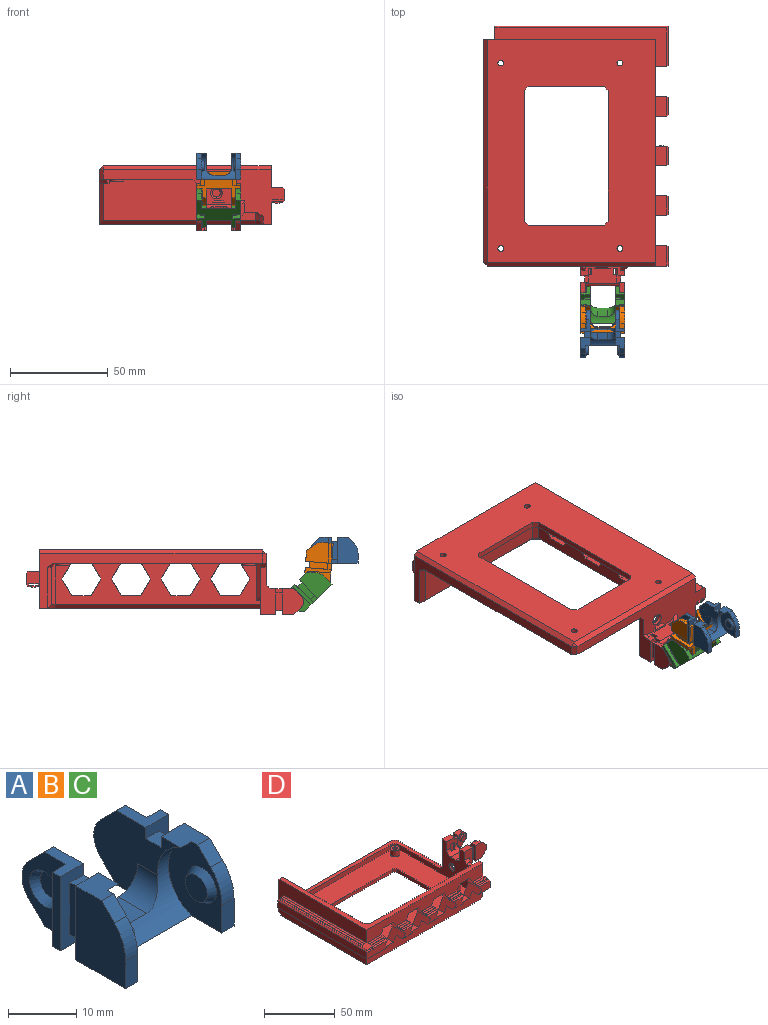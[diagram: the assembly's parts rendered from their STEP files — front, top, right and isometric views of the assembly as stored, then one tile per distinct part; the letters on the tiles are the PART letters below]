
ASSEMBLY  parts=4 mates=3
PART A: 54 faces, bbox 22.5x24.4x13.3 mm
  f0: plane 9.3x3.2mm, normal (-1,0,0), area 29.8mm2, adj f16,f17,f51,f53
  f1: plane 5.35x4.75mm, normal (0,0,1), area 22.5mm2, adj f4,f9,f17,f18,f40,f41
  f2: plane 9.3x3.2mm, normal (1,0,0), area 29.8mm2, adj f24,f25,f49,f52
  f3: plane 5.35x4.75mm, normal (0,0,1), area 22.5mm2, adj f5,f23,f24,f27,f39,f41
  f4: plane 18.07x13.3mm, normal (1,0,0), area 130.5mm2, adj f1,f6,f11,f16,f17,f19,f31,f32
  f5: plane 18.07x13.3mm, normal (-1,0,0), area 130.5mm2, adj f3,f6,f11,f24,f25,f26,f29,f30
  f6: plane 22.5x19.65mm, normal (0,0,-1), area 224.2mm2, adj f4,f5,f7,f8,f11,f13,f14,f15
  f7: plane 4.99x2.5mm, normal (0,-1,0), area 12.5mm2, adj f6,f23,f28,f39
  f8: plane 4.99x2.5mm, normal (0,-1,0), area 12.5mm2, adj f6,f10,f18,f40
  f9: plane 2.66x2.66mm, normal (0,-0.71,0.71), area 9.4mm2, adj f1,f10,f18,f40
  f10: cylinder r=8mm len=5.66mm, axis (1,0,0), area 15.7mm2, adj f8,f9,f18,f40
  f11: plane 13x6mm, normal (0,1,0), area 32.9mm2, adj f4,f5,f6,f12,f35,f36
  f12: plane 5.92x5mm, normal (0,0,1), area 29.6mm2, adj f11,f35,f36,f41
  f13: plane 13.3x9.1mm, normal (-1,0,0), area 67.8mm2, adj f6,f14,f19,f31,f32,f33,f44
  f14: plane 13.3x2.85mm, normal (0,1,0), area 37.9mm2, adj f6,f13,f15,f19
  f15: plane 13.3x1.7mm, normal (-1,0,0), area 22.6mm2, adj f6,f14,f16,f19
  f16: plane 13.3x4.75mm, normal (0,-1,0), area 36.1mm2, adj f0,f4,f6,f15,f19,f50,f51,f53
  f17: plane 13.3x4.75mm, normal (0,1,0), area 36.1mm2, adj f0,f1,f4,f6,f18,f50,f51,f53
  f18: plane 13.3x10.35mm, normal (-1,0,0), area 123.8mm2, adj f1,f6,f8,f9,f10,f17
  f19: plane 6.1x4.75mm, normal (0,0,1), area 16.4mm2, adj f4,f13,f14,f15,f16,f31
  f20: plane 13.3x1.7mm, normal (1,0,0), area 22.6mm2, adj f6,f21,f25,f26
  f21: plane 13.3x2.85mm, normal (0,1,0), area 37.9mm2, adj f6,f20,f22,f26
  f22: plane 13.3x9.1mm, normal (1,0,0), area 67.8mm2, adj f6,f21,f26,f29,f30,f34,f37
  f23: plane 13.3x10.35mm, normal (1,0,0), area 123.8mm2, adj f3,f6,f7,f24,f27,f28
  f24: plane 13.3x4.75mm, normal (0,1,0), area 36.1mm2, adj f2,f3,f5,f6,f23,f48,f49,f52
  f25: plane 13.3x4.75mm, normal (0,-1,0), area 36.1mm2, adj f2,f5,f6,f20,f26,f48,f49,f52
  f26: plane 6.1x4.75mm, normal (0,0,1), area 16.4mm2, adj f5,f20,f21,f22,f25,f29
  f27: plane 2.66x2.66mm, normal (0,-0.71,0.71), area 9.4mm2, adj f3,f23,f28,f39
  f28: cylinder r=8mm len=5.66mm, axis (1,0,0), area 15.7mm2, adj f7,f23,f27,f39
  f29: plane 3.33x3.33mm, normal (0,0.71,0.71), area 8.9mm2, adj f5,f22,f26,f34
  f30: plane 3.33x3.33mm, normal (0,0.71,-0.71), area 8.9mm2, adj f5,f6,f22,f34
  f31: plane 3.33x3.33mm, normal (0,0.71,0.71), area 8.9mm2, adj f4,f13,f19,f33
  f32: plane 3.33x3.33mm, normal (0,0.71,-0.71), area 8.9mm2, adj f4,f6,f13,f33
  f33: cylinder r=4.7mm len=6.65mm, axis (-1,0,0), area 14mm2, adj f4,f13,f31,f32
  f34: cylinder r=4.7mm len=6.65mm, axis (-1,0,0), area 14mm2, adj f5,f22,f29,f30
  f35: cylinder r=4mm len=5.92mm, axis (0,1,0), area 31.9mm2, adj f4,f11,f12,f41
  f36: cylinder r=4mm len=5.92mm, axis (0,-1,0), area 31.9mm2, adj f5,f11,f12,f41
  f37: cone r=3.1mm half-angle=30deg, axis (1,0,0), area 27.4mm2, adj f22,f38
  f38: plane 4.58x4.58mm, normal (1,0,0), area 16.5mm2, adj f37
  f39: plane 13.3x11.1mm, normal (-1,0,0), area 88.3mm2, adj f3,f6,f7,f27,f28,f41,f42
  f40: plane 13.3x11.1mm, normal (1,0,0), area 88.3mm2, adj f1,f6,f8,f9,f10,f41,f46
  f41: cylinder r=7mm len=17.5mm, axis (1,0,0), area 135.2mm2, adj f1,f3,f4,f5,f6,f12,f35,f36
  f42: cone r=3mm half-angle=30deg, axis (1,0,0), area 23.9mm2, adj f39,f43
  f43: plane 4.56x4.56mm, normal (-1,0,0), area 16.3mm2, adj f42
  f44: cone r=3.1mm half-angle=30deg, axis (-1,0,0), area 27.4mm2, adj f13,f45
  f45: plane 4.58x4.58mm, normal (-1,0,0), area 16.5mm2, adj f44
  f46: cone r=3mm half-angle=30deg, axis (-1,0,0), area 23.9mm2, adj f40,f47
  f47: plane 4.56x4.56mm, normal (1,0,0), area 16.3mm2, adj f46
  f48: plane 3.2x2mm, normal (1,0,0), area 6.4mm2, adj f6,f24,f25,f49
  f49: plane 3.2x2mm, normal (0,0,-1), area 6.4mm2, adj f2,f24,f25,f48
  f50: plane 3.2x2mm, normal (-1,0,0), area 6.4mm2, adj f6,f16,f17,f51
  f51: plane 3.2x2mm, normal (0,0,-1), area 6.4mm2, adj f0,f16,f17,f50
  f52: plane 3.2x2.75mm, normal (0,0,1), area 8.8mm2, adj f2,f5,f24,f25
  f53: plane 3.2x2.75mm, normal (0,0,1), area 8.8mm2, adj f0,f4,f16,f17
PART B: same geometry as A
PART C: same geometry as A
PART D: 229 faces, bbox 142.5x95.3x35.7 mm
  f0: plane 9.3x1.7mm, normal (1,0,0), area 11.3mm2, adj f1,f2,f8,f9,f10,f207,f212
  f1: plane 3.53x3.4mm, normal (0,-1,0), area 12mm2, adj f0,f8,f10,f208
  f2: plane 8.5x3.4mm, normal (0,1,0), area 28.9mm2, adj f0,f8,f208,f212
  f3: plane 3.53x3.4mm, normal (0,1,0), area 12mm2, adj f4,f8,f186,f210
  f4: plane 9.3x1.7mm, normal (1,0,0), area 11.3mm2, adj f3,f5,f8,f175,f186,f209,f211
  f5: plane 8.5x3.4mm, normal (0,-1,0), area 28.9mm2, adj f4,f8,f210,f211
  f6: plane 2.4x2mm, normal (0.71,0,-0.71), area 4mm2, adj f8,f43,f167,f221
  f7: plane 4.4x2mm, normal (0.71,0,-0.71), area 6.8mm2, adj f8,f43,f214,f222
  f8: plane 22.5x14.2mm, normal (0,0,-1), area 168.2mm2, adj f0,f1,f2,f3,f4,f5,f6,f7
  f9: plane 13.84x7.3mm, normal (0,1,0), area 64mm2, adj f0,f10,f18,f55,f168,f171,f172,f185
  f10: cylinder r=4mm len=12.06mm, axis (-1,0,0), area 62.5mm2, adj f0,f1,f9,f55,f178,f197,f198,f208
  f11: plane 2.5x0.03mm, normal (1,0,0), area 0.1mm2, adj f14,f15,f169,f194
  f12: plane 3.84x3.84mm, normal (0.71,0,0.71), area 13.6mm2, adj f14,f18,f169,f194
  f13: plane 3.84x3.84mm, normal (0.71,0,-0.71), area 13.6mm2, adj f8,f15,f169,f194
  f14: cylinder r=3.95mm len=2.79mm, axis (0,1,0), area 7.8mm2, adj f11,f12,f169,f194
  f15: cylinder r=3.95mm len=2.79mm, axis (0,1,0), area 7.8mm2, adj f11,f13,f169,f194
  f16: plane 9.3x3.2mm, normal (0,-1,0), area 29.8mm2, adj f168,f171,f184,f185
  f17: plane 9.3x3.2mm, normal (0,1,0), area 29.8mm2, adj f173,f174,f180,f182
  f18: plane 6.32x5.07mm, normal (0,0,1), area 25.1mm2, adj f9,f12,f168,f169,f193,f194,f196
  f19: plane 6.32x5.07mm, normal (0,0,1), area 25.1mm2, adj f173,f175,f176,f187,f191,f195,f202
  f20: plane 106x25mm, normal (0,1,0), area 1541.8mm2, adj f42,f67,f68,f69,f70,f71,f72,f73
  f21: plane 20.13x6mm, normal (0,-1,0), area 112.6mm2, adj f85,f90,f105,f106,f108,f141,f164,f165
  f22: plane 88x19.71mm, normal (0,0,1), area 380.6mm2, adj f23,f31,f40,f45,f90,f104,f106,f107
  f23: plane 13.83x0.2mm, normal (0,-0.71,0.71), area 3.9mm2, adj f22,f27,f90,f138
  f24: plane 10.25x0.2mm, normal (0,-0.71,0.71), area 2.9mm2, adj f28,f35,f84,f88
  f25: plane 10.25x0.2mm, normal (0,-0.71,0.71), area 2.9mm2, adj f29,f36,f73,f82
  f26: plane 10.25x0.2mm, normal (0,-0.71,0.71), area 2.9mm2, adj f30,f37,f72,f77
  f27: plane 13.83x2mm, normal (0,0,1), area 27.6mm2, adj f23,f31,f90,f138
  f28: plane 10.25x2mm, normal (0,0,1), area 20.5mm2, adj f24,f32,f84,f88
  f29: plane 10.25x2mm, normal (0,0,1), area 20.5mm2, adj f25,f33,f73,f82
  f30: plane 10.25x2mm, normal (0,0,1), area 20.5mm2, adj f26,f34,f72,f77
  f31: plane 13.83x0.2mm, normal (0,0.71,0.71), area 3.9mm2, adj f22,f27,f90,f138
  f32: plane 10.25x0.2mm, normal (0,0.71,0.71), area 2.9mm2, adj f28,f84,f88,f92
  f33: plane 10.25x0.2mm, normal (0,0.71,0.71), area 2.9mm2, adj f29,f73,f82,f95
  f34: plane 10.25x0.2mm, normal (0,0.71,0.71), area 2.9mm2, adj f30,f72,f77,f98
  f35: plane 10.02x1.6mm, normal (0,0,1), area 16mm2, adj f24,f84,f88,f110
  f36: plane 10.02x1.6mm, normal (0,0,1), area 16mm2, adj f25,f73,f82,f113
  f37: plane 10.02x1.6mm, normal (0,0,1), area 16mm2, adj f26,f72,f77,f114
  f38: plane 10.71x1.6mm, normal (0,0,1), area 17.1mm2, adj f43,f70,f117,f135
  f39: plane 116x88mm, normal (0,0,1), area 808mm2, adj f40,f43,f44,f45,f120,f122,f123
  f40: plane 116x11mm, normal (0,-1,0), area 1039.4mm2, adj f22,f39,f43,f45,f70,f71,f72,f73
  f41: plane 116x11mm, normal (0,-1,0), area 1037.4mm2, adj f43,f45,f54,f67,f68,f69,f74,f75
  f42: plane 107x79mm, normal (0,0,1), area 5246.1mm2, adj f20,f46,f47,f48,f52,f55,f56,f58
  f43: plane 93x28mm, normal (1,0,0), area 1006.8mm2, adj f6,f7,f8,f38,f39,f40,f41,f57
  f44: plane 114x28mm, normal (0,1,0), area 664.8mm2, adj f39,f45,f57,f119,f125,f126,f219
  f45: plane 88x30mm, normal (-1,0,0), area 1982mm2, adj f22,f39,f40,f41,f44,f54,f91,f104
  f46: plane 67x3mm, normal (0,1,0), area 201mm2, adj f42,f54,f131,f133
  f47: plane 39x3mm, normal (1,0,0), area 117mm2, adj f42,f54,f131,f132
  f48: plane 67x3mm, normal (0,-1,0), area 201mm2, adj f42,f54,f132,f134
  f49: cylinder r=1.5mm len=8mm, axis (0,0,1), area 75.4mm2, adj f54,f63
  f50: cylinder r=1.5mm len=8mm, axis (0,0,1), area 75.4mm2, adj f54,f61
  f51: cylinder r=1.5mm len=8mm, axis (0,0,1), area 75.4mm2, adj f54,f59
  f52: plane 39x3mm, normal (-1,0,0), area 117mm2, adj f42,f54,f133,f134
  f53: cylinder r=1.5mm len=8mm, axis (0,0,1), area 75.4mm2, adj f54,f65
  f54: plane 114x86mm, normal (0,0,-1), area 6730.7mm2, adj f41,f45,f46,f47,f48,f49,f50,f51
  f55: plane 75x30.3mm, normal (-1,0,0), area 854.9mm2, adj f9,f10,f42,f57,f118,f130,f166,f167
  f56: plane 103x4mm, normal (0,-1,0), area 412mm2, adj f42,f57,f129,f130
  f57: plane 109.17x48mm, normal (0,0,1), area 459.7mm2, adj f43,f44,f55,f56,f125,f130,f218,f219
  f58: cylinder r=3.5mm len=7mm, axis (0,0,-1), area 110mm2, adj f42,f59
  f59: plane 7x7mm, normal (0,0,1), area 31.4mm2, adj f51,f58
  f60: cylinder r=3.5mm len=7mm, axis (0,0,-1), area 110mm2, adj f42,f61
  f61: plane 7x7mm, normal (0,0,1), area 31.4mm2, adj f50,f60
  f62: cylinder r=3.5mm len=7mm, axis (0,0,-1), area 110mm2, adj f42,f63
  f63: plane 7x7mm, normal (0,0,1), area 31.4mm2, adj f49,f62
  f64: cylinder r=3.5mm len=7mm, axis (0,0,-1), area 110mm2, adj f42,f65
  f65: plane 7x7mm, normal (0,0,1), area 31.4mm2, adj f53,f64
  f66: plane 78x25mm, normal (1,0,0), area 1932mm2, adj f42,f119,f120,f121,f129,f220
  f67: plane 13x8.66mm, normal (0.87,0,0.5), area 91.8mm2, adj f20,f41,f68,f72,f99,f100,f115
  f68: plane 10x6mm, normal (0,0,1), area 60mm2, adj f20,f41,f67,f69
  f69: plane 13x8.66mm, normal (-0.87,0,0.5), area 91.8mm2, adj f20,f41,f68,f70,f102,f103,f116
  f70: plane 13x8.66mm, normal (-0.87,0,-0.5), area 86.5mm2, adj f20,f38,f40,f69,f71,f101,f103,f117
  f71: plane 10x6mm, normal (0,0,-1), area 60mm2, adj f20,f40,f70,f72
  f72: plane 13x8.66mm, normal (0.87,0,-0.5), area 86.5mm2, adj f20,f26,f30,f34,f37,f40,f67,f71
  f73: plane 13x8.66mm, normal (0.87,0,-0.5), area 86.5mm2, adj f20,f25,f29,f33,f36,f40,f74,f78
  f74: plane 13x8.66mm, normal (0.87,0,0.5), area 91.8mm2, adj f20,f41,f73,f75,f96,f97,f112
  f75: plane 10x6mm, normal (0,0,1), area 60mm2, adj f20,f41,f74,f76
  f76: plane 13x8.66mm, normal (-0.87,0,0.5), area 91.8mm2, adj f20,f41,f75,f77,f99,f100,f115
  f77: plane 13x8.66mm, normal (-0.87,0,-0.5), area 86.5mm2, adj f20,f26,f30,f34,f37,f40,f76,f78
  f78: plane 10x6mm, normal (0,0,-1), area 60mm2, adj f20,f40,f73,f77
  f79: plane 13x8.66mm, normal (0.87,0,0.5), area 91.8mm2, adj f20,f41,f80,f84,f93,f94,f111
  f80: plane 10x6mm, normal (0,0,1), area 60mm2, adj f20,f41,f79,f81
  f81: plane 13x8.66mm, normal (-0.87,0,0.5), area 91.8mm2, adj f20,f41,f80,f82,f96,f97,f112
  f82: plane 13x8.66mm, normal (-0.87,0,-0.5), area 86.5mm2, adj f20,f25,f29,f33,f36,f40,f81,f83
  f83: plane 10x6mm, normal (0,0,-1), area 60mm2, adj f20,f40,f82,f84
  f84: plane 13x8.66mm, normal (0.87,0,-0.5), area 86.5mm2, adj f20,f24,f28,f32,f35,f40,f79,f83
  f85: plane 13x8.66mm, normal (0.87,0,0.5), area 91.8mm2, adj f20,f21,f41,f86,f90,f91,f108
  f86: plane 10x6mm, normal (0,0,1), area 60mm2, adj f20,f41,f85,f87
  f87: plane 13x8.66mm, normal (-0.87,0,0.5), area 91.8mm2, adj f20,f41,f86,f88,f93,f94,f111
  f88: plane 13x8.66mm, normal (-0.87,0,-0.5), area 86.5mm2, adj f20,f24,f28,f32,f35,f40,f87,f89
  f89: plane 10x6mm, normal (0,0,-1), area 60mm2, adj f20,f40,f88,f90
  f90: plane 13x8.66mm, normal (0.87,0,-0.5), area 86.5mm2, adj f20,f21,f22,f23,f27,f31,f40,f85
  f91: plane 88x19.71mm, normal (0,0,-1), area 610.3mm2, adj f41,f45,f85,f104,f108,f109
  f92: plane 10.02x2mm, normal (0,0,1), area 20mm2, adj f32,f40,f84,f88
  f93: plane 10.02x6mm, normal (0,0,-1), area 60.1mm2, adj f41,f79,f87,f111
  f94: plane 8.86x6mm, normal (0,-1,0), area 42.8mm2, adj f79,f84,f87,f88,f110,f111
  f95: plane 10.02x2mm, normal (0,0,1), area 20mm2, adj f33,f40,f73,f82
  f96: plane 10.02x6mm, normal (0,0,-1), area 60.1mm2, adj f41,f74,f81,f112
  f97: plane 8.86x6mm, normal (0,-1,0), area 42.8mm2, adj f73,f74,f81,f82,f112,f113
  f98: plane 10.02x2mm, normal (0,0,1), area 20mm2, adj f34,f40,f72,f77
  f99: plane 10.02x6mm, normal (0,0,-1), area 60.1mm2, adj f41,f67,f76,f115
  f100: plane 8.86x6mm, normal (0,-1,0), area 42.8mm2, adj f67,f72,f76,f77,f114,f115
  f101: plane 10.71x2mm, normal (0,0,1), area 21.4mm2, adj f40,f43,f70,f137
  f102: plane 10.71x6mm, normal (0,0,-1), area 64.3mm2, adj f41,f43,f69,f116
  f103: plane 10.13x6mm, normal (0,-1,0), area 55.6mm2, adj f43,f69,f70,f116,f117
  f104: plane 8.2x7mm, normal (0,1,0), area 50.4mm2, adj f22,f45,f91,f105,f107,f109,f139,f141
  f105: plane 89x6mm, normal (-1,0,0), area 534mm2, adj f21,f104,f107,f109
  f106: plane 20.71x1mm, normal (0,-0.71,0.71), area 25.3mm2, adj f21,f22,f90,f107,f139,f164,f165
  f107: plane 89x1mm, normal (-0.71,0,0.71), area 125.2mm2, adj f22,f104,f105,f106
  f108: plane 20.71x1mm, normal (0,-0.71,-0.71), area 28.2mm2, adj f21,f85,f91,f109
  f109: plane 89x1mm, normal (-0.71,0,-0.71), area 125.2mm2, adj f91,f104,f105,f108
  f110: plane 10.02x1mm, normal (0,-0.71,0.71), area 13.4mm2, adj f35,f84,f88,f94
  f111: plane 10.02x1mm, normal (0,-0.71,-0.71), area 13.4mm2, adj f79,f87,f93,f94
  f112: plane 10.02x1mm, normal (0,-0.71,-0.71), area 13.4mm2, adj f74,f81,f96,f97
  f113: plane 10.02x1mm, normal (0,-0.71,0.71), area 13.4mm2, adj f36,f73,f82,f97
  f114: plane 10.02x1mm, normal (0,-0.71,0.71), area 13.4mm2, adj f37,f72,f77,f100
  f115: plane 10.02x1mm, normal (0,-0.71,-0.71), area 13.4mm2, adj f67,f76,f99,f100
  f116: plane 10.71x1mm, normal (0,-0.71,-0.71), area 14.7mm2, adj f43,f69,f102,f103
  f117: plane 10.71x1mm, normal (0,-0.71,0.71), area 14.7mm2, adj f38,f43,f70,f103
  f118: plane 23x2mm, normal (-0.71,0.71,0), area 62.2mm2, adj f20,f42,f55,f217
  f119: plane 21x2mm, normal (0.71,0.71,0), area 56.6mm2, adj f44,f66,f120,f219
  f120: plane 80x2mm, normal (0.71,0,0.71), area 223.4mm2, adj f39,f66,f119,f122
  f121: plane 25x2mm, normal (0.71,0.71,0), area 70.7mm2, adj f20,f42,f66,f122
  f122: plane 4x4mm, normal (0.58,0.58,0.58), area 10.4mm2, adj f39,f120,f121,f123
  f123: plane 108x2mm, normal (0,0.71,0.71), area 302.6mm2, adj f20,f39,f122,f124
  f124: plane 4x2mm, normal (0.71,0.71,0), area 8.5mm2, adj f20,f43,f123,f216
  f125: plane 5x2mm, normal (0.71,0.71,0), area 14.1mm2, adj f43,f44,f57,f127
  f126: plane 114x2mm, normal (0,0.71,-0.71), area 322.4mm2, adj f44,f45,f54,f127
  f127: plane 2x2mm, normal (0.58,0.58,-0.58), area 3.5mm2, adj f125,f126,f128
  f128: plane 86x2mm, normal (0.71,0,-0.71), area 243.2mm2, adj f41,f43,f54,f127
  f129: plane 6x2mm, normal (0.71,-0.71,0), area 14.1mm2, adj f42,f56,f66,f220
  f130: plane 4x2mm, normal (-0.71,-0.71,0), area 11.3mm2, adj f42,f55,f56,f57
  f131: plane 3x2mm, normal (0.71,0.71,0), area 8.5mm2, adj f42,f46,f47,f54
  f132: plane 3x2mm, normal (0.71,-0.71,0), area 8.5mm2, adj f42,f47,f48,f54
  f133: plane 3x2mm, normal (-0.71,0.71,0), area 8.5mm2, adj f42,f46,f52,f54
  f134: plane 3x2mm, normal (-0.71,-0.71,0), area 8.5mm2, adj f42,f48,f52,f54
  f135: plane 10.83x0.2mm, normal (0,-0.71,0.71), area 3mm2, adj f38,f43,f70,f136
  f136: plane 10.83x2mm, normal (0,0,1), area 21.6mm2, adj f43,f70,f135,f137
  f137: plane 10.83x0.2mm, normal (0,0.71,0.71), area 3mm2, adj f43,f70,f101,f136
  f138: plane 2.4x0.2mm, normal (-1,0,0), area 0.4mm2, adj f22,f23,f27,f31
  f139: plane 88.6x19.06mm, normal (0,0,-1), area 513.3mm2, adj f90,f104,f106,f140,f142,f163,f164,f165
  f140: plane 14.06x1mm, normal (0,1,0), area 13.8mm2, adj f90,f139,f141,f164
  f141: plane 89x18.49mm, normal (0,0,1), area 512.4mm2, adj f21,f90,f104,f140,f142,f163,f164,f165
  f142: plane 14.06x1mm, normal (0,-1,0), area 13.8mm2, adj f90,f139,f141,f163
  f143: plane 9.33x5mm, normal (0,0,-1), area 46.6mm2, adj f84,f88,f144,f146
  f144: plane 9.33x1mm, normal (0,1,0), area 8.7mm2, adj f84,f88,f143,f145
  f145: plane 8.17x5mm, normal (0,0,1), area 40.9mm2, adj f84,f88,f144,f146
  f146: plane 9.33x1mm, normal (0,-1,0), area 8.7mm2, adj f84,f88,f143,f145
  f147: plane 9.33x5mm, normal (0,0,-1), area 46.6mm2, adj f73,f82,f148,f150
  f148: plane 9.33x1mm, normal (0,1,0), area 8.7mm2, adj f73,f82,f147,f149
  f149: plane 8.17x5mm, normal (0,0,1), area 40.9mm2, adj f73,f82,f148,f150
  f150: plane 9.33x1mm, normal (0,-1,0), area 8.7mm2, adj f73,f82,f147,f149
  f151: plane 9.33x5mm, normal (0,0,-1), area 46.6mm2, adj f72,f77,f152,f154
  f152: plane 9.33x1mm, normal (0,1,0), area 8.7mm2, adj f72,f77,f151,f153
  f153: plane 8.17x5mm, normal (0,0,1), area 40.9mm2, adj f72,f77,f152,f154
  f154: plane 9.33x1mm, normal (0,-1,0), area 8.7mm2, adj f72,f77,f151,f153
  f155: plane 10.36x1mm, normal (0,-1,0), area 10.1mm2, adj f43,f70,f156,f158
  f156: plane 9.79x5mm, normal (0,0,1), area 48.9mm2, adj f43,f70,f155,f157
  f157: plane 10.36x1mm, normal (0,1,0), area 10.1mm2, adj f43,f70,f156,f158
  f158: plane 10.36x5mm, normal (0,0,-1), area 51.8mm2, adj f43,f70,f155,f157
  f159: plane 2.4x0.2mm, normal (0,-1,0), area 0.4mm2, adj f22,f160,f161,f162
  f160: plane 82x0.2mm, normal (-0.71,0,0.71), area 23.2mm2, adj f22,f104,f159,f161
  f161: plane 82x2mm, normal (0,0,1), area 164mm2, adj f104,f159,f160,f162
  f162: plane 82x0.2mm, normal (0.71,0,0.71), area 23.2mm2, adj f22,f104,f159,f161
  f163: plane 82.7x1mm, normal (-1,0,0), area 82.7mm2, adj f104,f139,f141,f142
  f164: plane 1.3x1mm, normal (-1,0,0), area 1.2mm2, adj f21,f106,f139,f140,f141
  f165: plane 89x1mm, normal (1,0,0), area 88.9mm2, adj f21,f104,f106,f139,f141
  f166: plane 13.3x8mm, normal (0,-1,0), area 76.4mm2, adj f8,f55,f171,f172,f213,f214
  f167: plane 24.3x8mm, normal (0,1,0), area 141.4mm2, adj f6,f8,f43,f55,f174,f177,f218
  f168: plane 13.3x4.75mm, normal (-1,0,0), area 36.1mm2, adj f8,f9,f16,f18,f169,f183,f184,f185
  f169: plane 13.3x11mm, normal (0,-1,0), area 120.6mm2, adj f8,f11,f12,f13,f14,f15,f18,f168
  f170: plane 2.5x0.03mm, normal (1,0,0), area 0.1mm2, adj f176,f189,f190,f195
  f171: plane 13.3x4.75mm, normal (1,0,0), area 36.1mm2, adj f8,f9,f16,f166,f172,f183,f184,f185
  f172: plane 8x4.75mm, normal (0,0,1), area 38mm2, adj f9,f55,f166,f171
  f173: plane 13.3x4.75mm, normal (-1,0,0), area 36.1mm2, adj f8,f17,f19,f175,f176,f180,f181,f182
  f174: plane 13.3x4.75mm, normal (1,0,0), area 36.1mm2, adj f8,f17,f167,f175,f177,f180,f181,f182
  f175: plane 13.84x7.3mm, normal (0,-1,0), area 64mm2, adj f4,f19,f55,f173,f174,f177,f180,f186
  f176: plane 13.3x11mm, normal (0,1,0), area 120.6mm2, adj f8,f19,f170,f173,f187,f188,f189,f190
  f177: plane 8x4.75mm, normal (0,0,1), area 38mm2, adj f55,f167,f174,f175
  f178: plane 12.06x5mm, normal (0,0,1), area 60.3mm2, adj f10,f55,f186,f199
  f179: plane 6.67x3mm, normal (0,0,1), area 17.2mm2, adj f43,f55,f213,f216,f217
  f180: plane 3.2x2.75mm, normal (0,0,1), area 8.8mm2, adj f17,f173,f174,f175
  f181: plane 3.2x2mm, normal (0,1,0), area 6.4mm2, adj f8,f173,f174,f182
  f182: plane 3.2x2mm, normal (0,0,-1), area 6.4mm2, adj f17,f173,f174,f181
  f183: plane 3.2x2mm, normal (0,-1,0), area 6.4mm2, adj f8,f168,f171,f184
  f184: plane 3.2x2mm, normal (0,0,-1), area 6.4mm2, adj f16,f168,f171,f183
  f185: plane 3.2x2.75mm, normal (0,0,1), area 8.8mm2, adj f9,f16,f168,f171
  f186: cylinder r=4mm len=12.06mm, axis (1,0,0), area 62.5mm2, adj f3,f4,f55,f175,f178,f200,f201,f210
  f187: plane 3.84x3.84mm, normal (0.71,0,0.71), area 13.6mm2, adj f19,f176,f189,f195
  f188: plane 3.84x3.84mm, normal (0.71,0,-0.71), area 13.6mm2, adj f8,f176,f190,f195
  f189: cylinder r=3.95mm len=2.79mm, axis (0,1,0), area 7.8mm2, adj f170,f176,f187,f195
  f190: cylinder r=3.95mm len=2.79mm, axis (0,1,0), area 7.8mm2, adj f170,f176,f188,f195
  f191: cylinder r=7mm len=11.13mm, axis (0,1,0), area 22mm2, adj f19,f192,f195,f201,f202
  f192: cylinder r=1.33mm len=17.5mm, axis (0,1,0), area 39.4mm2, adj f8,f191,f193,f194,f195,f198,f199,f200
  f193: cylinder r=7mm len=11.13mm, axis (0,1,0), area 22mm2, adj f18,f192,f194,f196,f197
  f194: plane 13.3x11.1mm, normal (0,1,0), area 79.1mm2, adj f8,f11,f12,f13,f14,f15,f18,f192
  f195: plane 13.3x11.1mm, normal (0,-1,0), area 79.1mm2, adj f8,f19,f170,f187,f188,f189,f190,f191
  f196: torus R=7.9mm, axis (0,-1,0), area 12.5mm2, adj f9,f18,f193,f197
  f197: bspline ~4.84x3.3mm, area 5.8mm2, adj f10,f193,f196,f198
  f198: bspline ~2.3x1.9mm, area 3.3mm2, adj f10,f192,f197,f199
  f199: cylinder r=0.9mm len=5mm, axis (0,1,0), area 9.6mm2, adj f178,f192,f198,f200
  f200: bspline ~2.55x1.92mm, area 3.3mm2, adj f186,f192,f199,f201
  f201: bspline ~5.04x3.79mm, area 5.8mm2, adj f186,f191,f200,f202
  f202: torus R=7.9mm, axis (0,1,0), area 12.5mm2, adj f19,f175,f191,f201
  f203: cone r=3mm half-angle=30deg, axis (0,1,0), area 23.9mm2, adj f195,f204
  f204: plane 4.56x4.56mm, normal (0,-1,0), area 16.3mm2, adj f203
  f205: cone r=3mm half-angle=30deg, axis (0,-1,0), area 23.9mm2, adj f194,f206
  f206: plane 4.56x4.56mm, normal (0,1,0), area 16.3mm2, adj f205
  f207: plane 3.4x0.05mm, normal (0,0,-1), area 0.2mm2, adj f0,f9,f208,f212
  f208: plane 9.3x1.7mm, normal (-1,0,0), area 11.3mm2, adj f1,f2,f8,f9,f10,f207,f212
  f209: plane 3.4x0.05mm, normal (0,0,-1), area 0.2mm2, adj f4,f175,f210,f211
  f210: plane 9.3x1.7mm, normal (-1,0,0), area 11.3mm2, adj f3,f5,f8,f175,f186,f209,f211
  f211: plane 3.4x0.8mm, normal (0,-0.71,-0.71), area 3.8mm2, adj f4,f5,f209,f210
  f212: plane 3.4x0.8mm, normal (0,0.71,-0.71), area 3.8mm2, adj f0,f2,f207,f208
  f213: plane 5x2mm, normal (0,-0.71,0.71), area 11.3mm2, adj f55,f166,f179,f214
  f214: plane 8x2mm, normal (0.71,-0.71,0), area 17mm2, adj f7,f43,f166,f213
  f215: plane 6.3x1mm, normal (0.71,0,-0.71), area 7.5mm2, adj f43,f223,f224,f225
  f216: plane 4x2mm, normal (0.5,0.5,0.71), area 6.3mm2, adj f43,f124,f179,f217
  f217: plane 3.83x2mm, normal (0,0.71,0.71), area 6.8mm2, adj f20,f118,f179,f216
  f218: plane 3x2mm, normal (0,0.71,0.71), area 8.5mm2, adj f43,f55,f57,f167
  f219: plane 4x2mm, normal (0.5,0.5,0.71), area 6.3mm2, adj f44,f57,f119,f220
  f220: plane 3.83x2mm, normal (0.71,0,0.71), area 6.8mm2, adj f57,f66,f129,f219
  f221: plane 2x2mm, normal (0,-0.71,-0.71), area 2.8mm2, adj f6,f8,f43
  f222: plane 2x2mm, normal (0,0.71,-0.71), area 2.8mm2, adj f7,f8,f43
  f223: plane 2x2mm, normal (0,-0.71,-0.71), area 2.1mm2, adj f8,f43,f215,f224
  f224: plane 8.3x1mm, normal (1,0,0), area 7.3mm2, adj f8,f215,f223,f225
  f225: plane 2x2mm, normal (0,0.71,-0.71), area 2.1mm2, adj f8,f43,f215,f224
  f226: cylinder r=2mm len=4mm, axis (1,0,0), area 12.6mm2, adj f227,f228
  f227: cone r=2mm half-angle=45deg, axis (-1,0,0), area 22.2mm2, adj f55,f226
  f228: cone r=2mm half-angle=45deg, axis (1,0,0), area 22.2mm2, adj f43,f226
PLACE A t=(-2.26,57.5,37.58)mm
PLACE B rot(axis=(-1,0,0),85.4deg) t=(-2.26,70.19,47.78)mm
PLACE C rot(axis=(-1,0,0),44.7deg) t=(-2.26,70.82,26.88)mm
PLACE D rot(axis=(-0.71,0.71,0),180deg) t=(-35.26,161.07,41.45)mm
MATE revolute A.f37 <-> B.f41  axis (1,0,0) through (-13.51,77.15,44.23)mm
MATE revolute B.f37 <-> C.f41  axis (1,0,0) through (-13.51,78.41,28.73)mm
MATE revolute C.f37 <-> D.f191  axis (1,0,0) through (-13.51,89.47,17.8)mm
